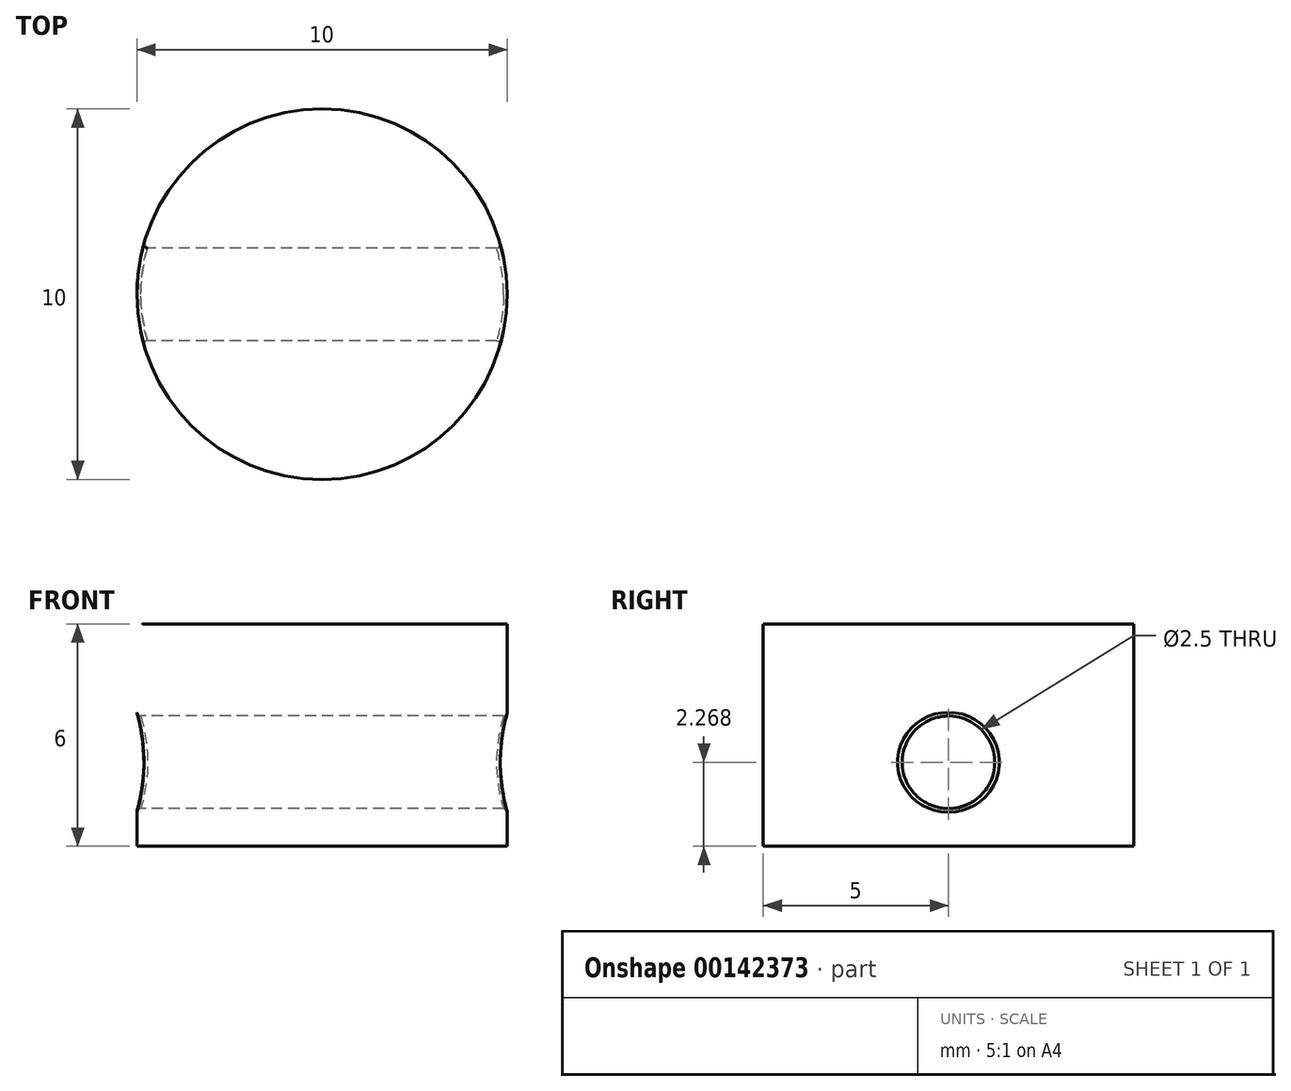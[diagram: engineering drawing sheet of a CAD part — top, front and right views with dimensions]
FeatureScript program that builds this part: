
annotation { "Feature Type Name" : "Feature", "Feature Type Description" : "" }
export const myFeature = defineFeature(function(context is Context, id is Id, definition is map)
    precondition{}
    {
        {
            var Q0;
            Q0=qCreatedBy(makeId("Front.planeOp"),FACE);
            var sketch = newSketch(context, id + "F0", { "sketchPlane" : qUnion([Q0])});
            skLineSegment(sketch, "E0", {"start": v(0, 0) * mm, "end": v(-5, 0) * mm});
            skLineSegment(sketch, "E1", {"start": v(-5, 0) * mm, "end": v(-5, 6) * mm});
            skLineSegment(sketch, "E2", {"start": v(-5, 6) * mm, "end": v(0, 6) * mm});
            skFitSpline(sketch, "E3", {"points": [v(-5, 6) * mm, v(-32.3, 16.63) * mm], "startDerivative": vector(-29.12, 3.13) * mm, "endDerivative": vector(-29.96, 19.74) * mm});
            skFitSpline(sketch, "E4.0", {"points": [v(-5, 4.1) * mm, v(-7.48, 4.48) * mm, v(-12.25, 5.55) * mm, v(-19, 8.14) * mm, v(-25.65, 11.8) * mm, v(-30.2, 15.01) * mm, v(-32.55, 16.82) * mm]});
            skLineSegment(sketch, "E5", {"start": v(0, 6) * mm, "end": v(0, 0) * mm});
            skSolve(sketch);
        }
        {
            var Q0;
            {var subQ0=sQuery(id+"F0.wireOp",EDGE,"E3");Q0=makeQuery(id+"F0.imprint","IMPRINT",FACE,{"disambiguationData":[TD([[makeQuery(id+"F0.imprint","IMPRINT",EDGE,{"derivedFrom":subQ0}),1.0]])]});}
            var Q1;
            {var subQ3=sQuery(id+"F0.wireOp",EDGE,"E0");Q1=makeQuery(id+"F0.imprint","IMPRINT",FACE,{"disambiguationData":[TD([[makeQuery(id+"F0.imprint","IMPRINT",EDGE,{"derivedFrom":subQ3}),-1.0]])]});}
            var Q2;
            Q2=sQuery(id+"F0.wireOp",EDGE,"E5");
            revolve(context, id + "F1", {"entities" : qUnion([Q0, Q1]), "axis" : qUnion([Q2]), "revolveType" : RevolveType.FULL});
        }
        {
            var Q0;
            Q0=sQuery(id+"F0.wireOp",EDGE,"E1");
            cPlane(context, id + "F2", {"entities" : qUnion([Q0]), "cplaneType" : CPlaneType.LINE_ANGLE, "offset" : 25 * mm, "angle" : 0 * degree, "width" : 150 * mm, "height" : 150 * mm});
        }
        {
            var Q0;
            Q0=qCreatedBy(id+"F2.planeOp",FACE);
            var sketch = newSketch(context, id + "F3", { "sketchPlane" : qUnion([Q0])});
            skCircle(sketch, "E6", {"center": v(0, 2.27) * mm, "radius": 1.25 * mm});
            skSolve(sketch);
        }
        {
            var Q0;
            Q0 = qSketchRegion(id + "F3", true);
            extrude(context, id + "F4", {"entities" : qUnion([Q0]), "operationType" : NewBodyOperationType.REMOVE, "endBound" : BoundingType.THROUGH_ALL, "depth" : 25 * mm});
        }
        {
            var Q0;
            Q0=makeQuery(id+"F4.boolean.opBoolean","INTERSECT",EDGE,{"disambiguationData":[OD(0.0)],"derivedFrom":[makeQuery(id+"F1.opRevolve","SWEPT_FACE",FACE,{"disambiguationData":[OSD([sQuery(id+"F0.wireOp",EDGE,"E1")])]}),makeQuery(id+"F4.opExtrude","SWEPT_FACE",FACE,{"disambiguationData":[OSD([sQuery(id+"F3.wireOp",EDGE,"E6")])]})]});
            var Q1;
            Q1=makeQuery(id+"F4.boolean.opBoolean","INTERSECT",EDGE,{"disambiguationData":[OD(1.0)],"derivedFrom":[makeQuery(id+"F1.opRevolve","SWEPT_FACE",FACE,{"disambiguationData":[OSD([sQuery(id+"F0.wireOp",EDGE,"E1")])]}),makeQuery(id+"F4.opExtrude","SWEPT_FACE",FACE,{"disambiguationData":[OSD([sQuery(id+"F3.wireOp",EDGE,"E6")])]})]});
            fillet(context, id + "F5", {"entities" : qUnion([Q0, Q1]), "radius" : .1 * mm, "tangentPropagation" : true, "allowEdgeOverflow" : false});
        }
    });
